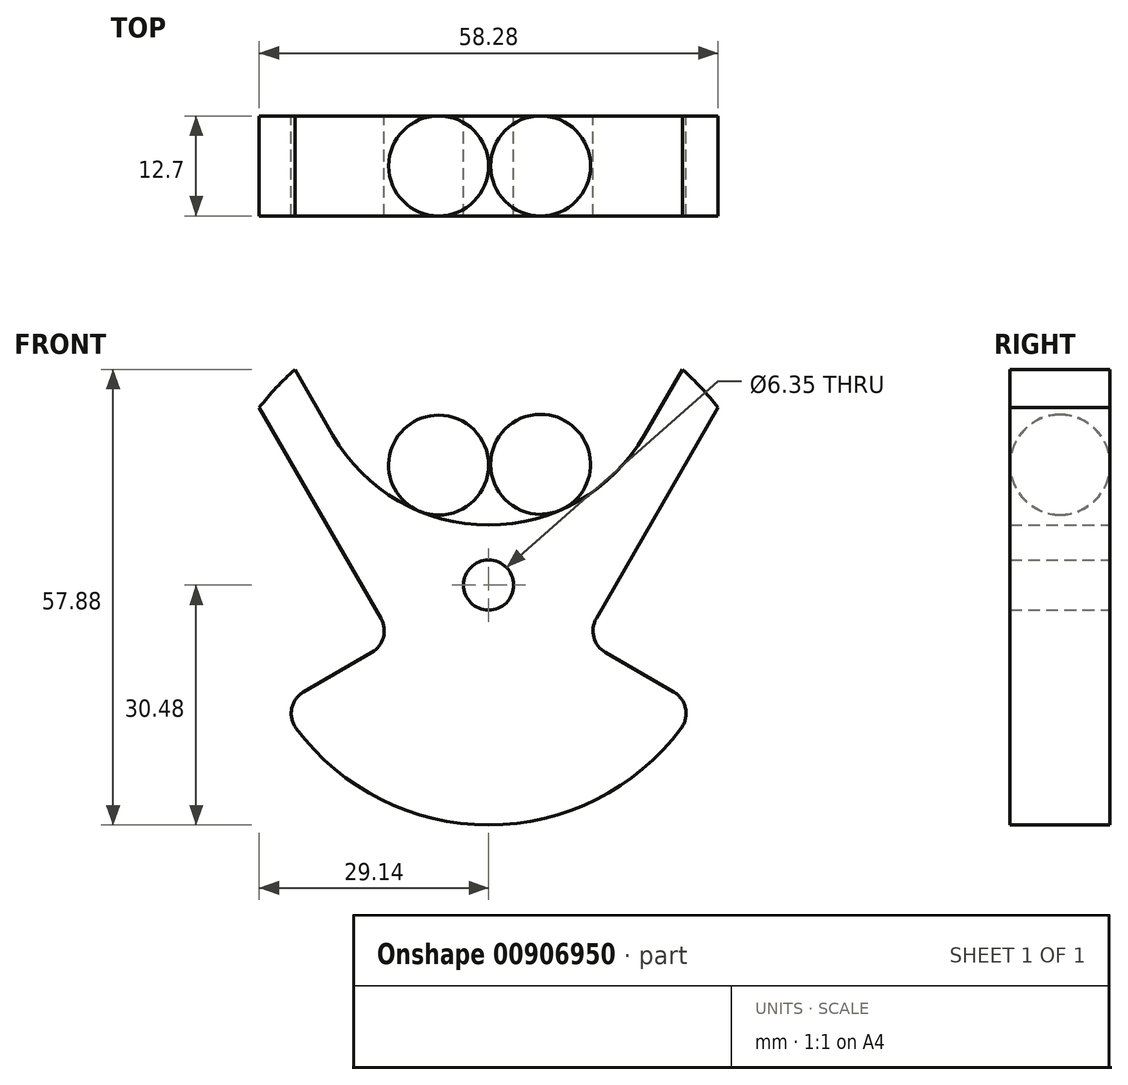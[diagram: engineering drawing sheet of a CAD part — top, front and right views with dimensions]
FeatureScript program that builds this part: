
annotation { "Feature Type Name" : "Feature", "Feature Type Description" : "" }
export const myFeature = defineFeature(function(context is Context, id is Id, definition is map)
    precondition{}
    {
        {
            var Q0;
            Q0=qCreatedBy(makeId("Front.planeOp"),FACE);
            var sketch = newSketch(context, id + "F0", { "sketchPlane" : qUnion([Q0])});
            skCircle(sketch, "E0", {"center": v(0, 0) * mm, "radius": 3.18 * mm});
            skLineSegment(sketch, "E1", {"start": v(0, 0) * mm, "end": v(0, 57) * mm, "construction": true});
            skArc(sketch, "E2", {"start": v(29.14, 22.53) * mm, "mid": v(26.99, 25.06) * mm, "end": v(24.62, 27.4) * mm});
            skCircle(sketch, "E3", {"center": v(0, 0) * mm, "radius": 7.62 * mm, "construction": true});
            skLineSegment(sketch, "E4", {"start": v(19.8, 19.05) * mm, "end": v(24.62, 27.4) * mm});
            skLineSegment(sketch, "E5.0", {"start": v(13.69, -4.24) * mm, "end": v(29.14, 22.53) * mm});
            skLineSegment(sketch, "E6", {"start": v(14.85, -8.57) * mm, "end": v(23.49, -13.56) * mm});
            skArc(sketch, "E7", {"start": v(0, 7.62) * mm, "mid": v(11.43, 10.68) * mm, "end": v(19.8, 19.05) * mm});
            skArc(sketch, "E8.MirrorCS", {"start": v(0, 7.62) * mm, "mid": v(-11.43, 10.68) * mm, "end": v(-19.8, 19.05) * mm});
            skLineSegment(sketch, "E9.MirrorCS", {"start": v(-19.8, 19.05) * mm, "end": v(-24.62, 27.4) * mm});
            skArc(sketch, "E10.MirrorCS", {"start": v(-29.14, 22.53) * mm, "mid": v(-26.99, 25.06) * mm, "end": v(-24.62, 27.4) * mm});
            skLineSegment(sketch, "E11.MirrorCS", {"start": v(-13.69, -4.24) * mm, "end": v(-29.14, 22.53) * mm});
            skLineSegment(sketch, "E12.MirrorCS", {"start": v(-14.85, -8.57) * mm, "end": v(-23.49, -13.56) * mm});
            skArc(sketch, "E13.trimOffspring", {"start": v(-24.45, -18.2) * mm, "mid": v(0, -30.48) * mm, "end": v(24.45, -18.2) * mm});
            skPoint(sketch, "E14.orphan", {"position": v(6.6, -3.81) * mm});
            skPoint(sketch, "E15.orphan", {"position": v(-6.6, -3.81) * mm});
            skPoint(sketch, "E16.visualSharp", {"position": v(-12.1, -6.99) * mm});
            skArc(sketch, "E16.filletArc", {"start": v(-14.85, -8.57) * mm, "mid": v(-13.37, -6.64) * mm, "end": v(-13.69, -4.24) * mm});
            skPoint(sketch, "E17.visualSharp", {"position": v(12.1, -6.99) * mm});
            skArc(sketch, "E17.filletArc", {"start": v(13.69, -4.24) * mm, "mid": v(13.37, -6.64) * mm, "end": v(14.85, -8.57) * mm});
            skLineSegment(sketch, "E18", {"start": v(0, 0) * mm, "end": v(25.4, 0) * mm, "construction": true});
            skLineSegment(sketch, "E19", {"start": v(25.4, 0) * mm, "end": v(25.4, -25.4) * mm, "construction": true});
            skLineSegment(sketch, "E20", {"start": v(25.4, -25.4) * mm, "end": v(50.8, -25.4) * mm, "construction": true});
            skCircle(sketch, "E21", {"center": v(50.8, -25.4) * mm, "radius": 5.72 * mm, "construction": true});
            skLineSegment(sketch, "E22", {"start": v(50.8, -25.4) * mm, "end": v(38.35, -25.4) * mm, "construction": true});
            skLineSegment(sketch, "E23", {"start": v(38.35, -25.4) * mm, "end": v(38.35, -19.02) * mm, "construction": true});
            skLineSegment(sketch, "E24", {"start": v(38.35, -19.02) * mm, "end": v(51.1, -19.7) * mm, "construction": true});
            skPoint(sketch, "E25.visualSharp", {"position": v(26.4, -15.24) * mm});
            skArc(sketch, "E25.filletArc", {"start": v(24.45, -18.2) * mm, "mid": v(25, -15.67) * mm, "end": v(23.49, -13.56) * mm});
            skPoint(sketch, "E26.visualSharp", {"position": v(-26.4, -15.24) * mm});
            skArc(sketch, "E26.filletArc", {"start": v(-23.49, -13.56) * mm, "mid": v(-25, -15.67) * mm, "end": v(-24.45, -18.2) * mm});
            skSolve(sketch);
        }
        {
            var Q0;
            Q0 = qSketchRegion(id + "F0", true);
            extrude(context, id + "F1", {"entities" : qUnion([Q0]), "endBound" : BoundingType.SYMMETRIC, "depth" : 12.7 * mm, "offsetDistance" : 25.4 * mm});
        }
        {
            var Q0;
            Q0=qCreatedBy(makeId("Front.planeOp"),FACE);
            var sketch = newSketch(context, id + "F2", { "sketchPlane" : qUnion([Q0])});
            skArc(sketch, "E27", {"start": v(6.6, 21.7) * mm, "mid": v(0.24, 15.34) * mm, "end": v(6.6, 9) * mm});
            skLineSegment(sketch, "E28", {"start": v(6.6, 9) * mm, "end": v(6.6, 21.7) * mm});
            skSolve(sketch);
        }
        {
            var Q0;
            Q0 = qSketchRegion(id + "F2", true);
            var Q1;
            Q1=sQuery(id+"F2.wireOp",EDGE,"E28");
            revolve(context, id + "F3", {"surfaceOperationType" : NewSurfaceOperationType.NEW, "entities" : qUnion([Q0]), "axis" : qUnion([Q1]), "revolveType" : RevolveType.FULL});
        }
        {
            var Q0;
            Q0=qCreatedBy(makeId("Front.planeOp"),FACE);
            var sketch = newSketch(context, id + "F4", { "sketchPlane" : qUnion([Q0])});
            skArc(sketch, "E29", {"start": v(-6.35, 8.9) * mm, "mid": v(0, 15.24) * mm, "end": v(-6.35, 21.6) * mm});
            skLineSegment(sketch, "E30", {"start": v(-6.35, 21.6) * mm, "end": v(-6.35, 8.9) * mm});
            skSolve(sketch);
        }
        {
            var Q0;
            Q0 = qSketchRegion(id + "F4", true);
            var Q1;
            Q1=sQuery(id+"F4.wireOp",EDGE,"E30");
            revolve(context, id + "F5", {"surfaceOperationType" : NewSurfaceOperationType.NEW, "entities" : qUnion([Q0]), "axis" : qUnion([Q1]), "revolveType" : RevolveType.FULL});
        }
    });
